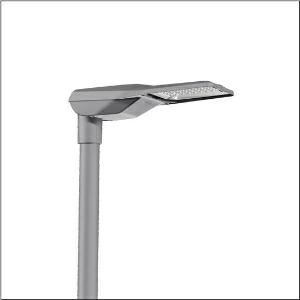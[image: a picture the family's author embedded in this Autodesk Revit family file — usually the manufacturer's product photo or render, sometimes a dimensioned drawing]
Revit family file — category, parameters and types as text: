
# Revit family: streetlight_sl_21_iq_mini___st1_0a_5xe2d31d08jb_a4dc
name_source: partatom
category: Lighting Fixtures
units: mm (PartAtom-declared; Revit-internal decimal feet)

## family parameters
Cut with Voids When Loaded = No
Host = Face
Light Source = No
Part Type = Normal
Room Calculation Point = No
Round Connector Dimension = Use Diameter
Shared = No

## types (1)
- --- (1 x LED, 10820 lm, 71.6 W, 3000K)
    Apparent Load = 72 VA
    CIE Flux Codes = 40 73 97 100 100
    Color Rendering = 70
    Color Temperature = 3000K
    Default Elevation = 1800 mm
    Description = Streetlight SL 21 iQ mini, mast luminaire, primary light control with lens, of PMMA, primary optical cover: cover, of toughened safety glass, transparent, light distribution: ST1.0a, light emission: direct distribution, primary light characteristic: asymmetric, installation type: post-top, side-entry, LED, High Power LED, rated luminous flux: 10.820lm, luminous efficacy: 151lm/W, light colour: 730, colour temperature: 3000K, control: Auto-Match, Temp-Guard, Lumen-Switch, Night-Set, Smart-Wire, Light-Fading, Desk-Remote (wireless, voltage-free reading and setting of iQ features in the workshop via application-optimized NFC function/RFID function), optimised constant luminous flux control (CLO 2.0), presetting dimming linear, mains connection: 220..240V, AC, 50/60Hz, start of lifetime: 72W, end of service life: 75W, reduction: 33W, luminaire housing, of diecast aluminium, powder-coated, Siteco® metallic grey (DB 702S), corrosivity category C5 mid according to DIN EN ISO 12944, please order mast flange separately, inclination adjustable: 0°, 5°, 10°, 15°, sealing non-destructively replaceable, multi-level sealing system, length: 628mm, width: 235mm, height: 110mm, mast flange for spigot size: 42mm (side-entry): 5XC10008XM4, 60/48mm (side-entry/post-top): 5XC10108XM2, 76/60mm (side-entry/post-top): 5XC10108XM1, protection rating (complete): IP66, insulation class (complete): insulation class II (safety insulation), certification: CE, ENEC, ENEC+, VDE, impact resistance: IK09, permissible operating ambient temperature for outdoor applications: -40..+50°C, standard-compliant lighting for roads and squares, packaging unit: 1 piece

Light Distribution: ST1.0a
    Height = 110 mm
    Lamp = 1 x LED
    Lamp Light Flux = 10820 lm
    Lamp Power = 71.6 W
    Lamp count = 1
    Length = 625 mm
    Luminous efficacy = 151 lm/W
    Manufacturer = Siteco
    ModVariant = No
    Model = 5XE2D31D08JB
    Number of Poles = 1
    OnlyDefault = Yes
    Power Factor = 1
    Product Name = Streetlight SL 21 iQ mini | ST1.0a
    Product group = mast luminaire | pylon top
    ProductGroupID = 6100
    Protection Class = Protection class II
    Protection Degree = IP 66
    RLX_Detail_Level = 1
    RLX_Emergency_Light_Flux = 0 lm
    RLX_Emergency_Type = 0
    RLX_Emergency_Type_DB = No
    RlxData = <blob elided: 92305 chars, md5=6e865512>
    Socket = socket
    Standby Power = 0 W
    System Light Flux = 10820 lm
    System Power = 72 W
    Type Comments = factory setting: luminous flux: 100 % | dim-lin: 254 | 746 mA
    Type Image = l_1003519.jpg
    URL = http://relux.com
    VarID = @adj_104123
    Voltage = 0 V
    Weight = 0.00 kg
    Width = 234 mm

## geometry (parser evidence)
native form markers: Blend x4, Sweep x9
no freeform markers — native parametric forms only
